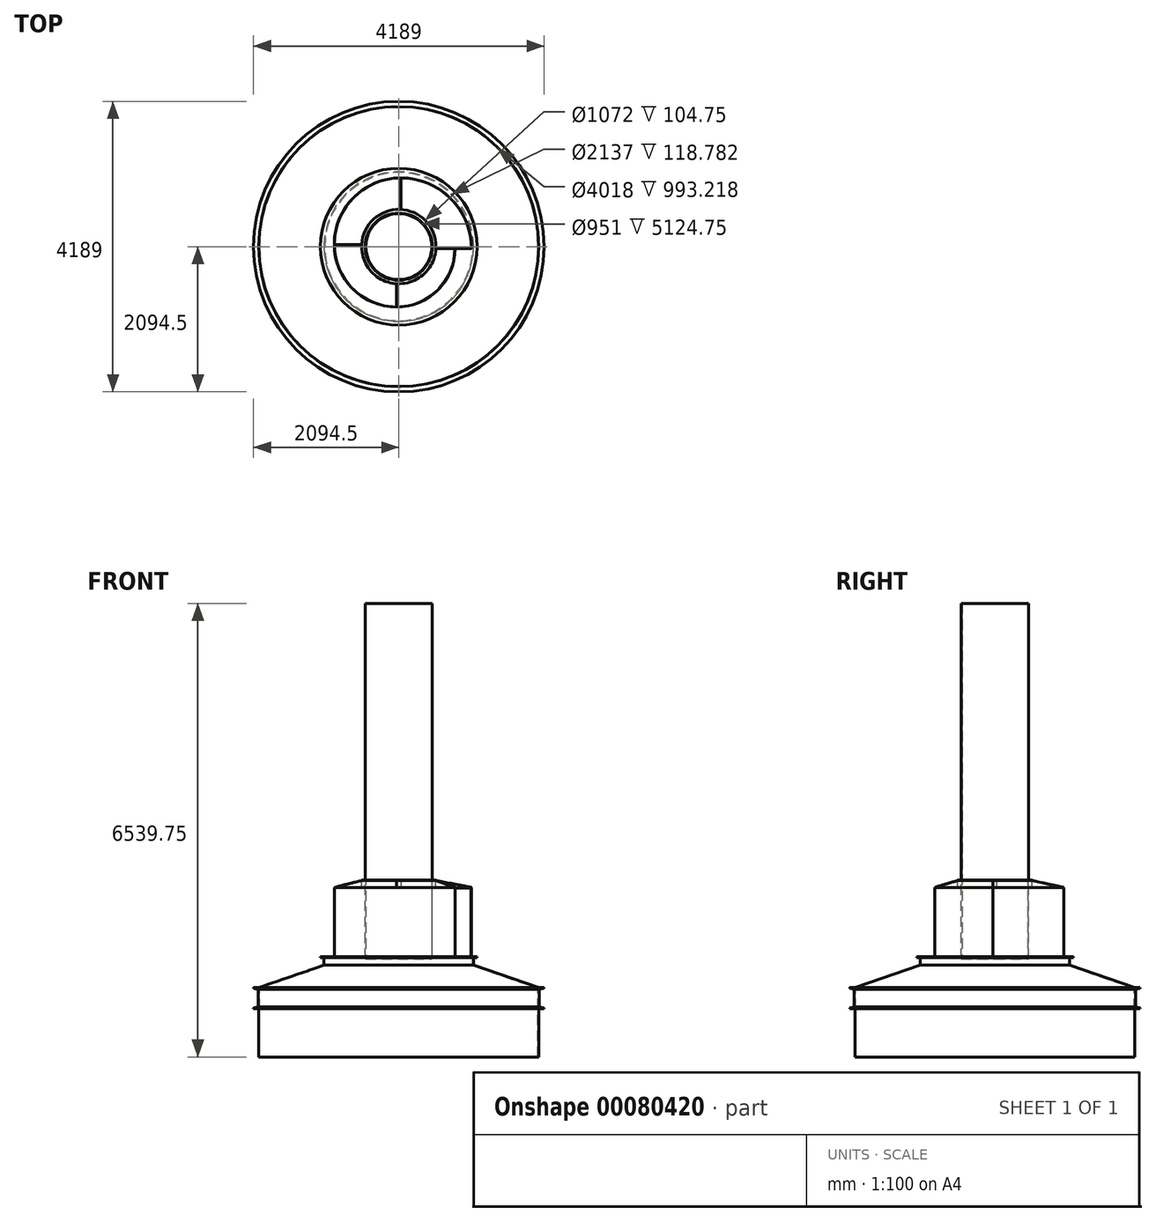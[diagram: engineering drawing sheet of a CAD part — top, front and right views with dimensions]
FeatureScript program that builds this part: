
annotation { "Feature Type Name" : "Feature", "Feature Type Description" : "" }
export const myFeature = defineFeature(function(context is Context, id is Id, definition is map)
    precondition{}
    {
        {
            var Q0;
            Q0=qCreatedBy(makeId("Front.planeOp"),FACE);
            var sketch = newSketch(context, id + "F0", { "sketchPlane" : qUnion([Q0])});
            skLineSegment(sketch, "E0", {"start": v(-2018.5, -1000) * mm, "end": v(-2018.5, 0) * mm});
            skLineSegment(sketch, "E1", {"start": v(-2018.5, 0) * mm, "end": v(-1078, 323) * mm});
            skLineSegment(sketch, "E2", {"start": v(-1078, 323) * mm, "end": v(-1078, 435) * mm});
            skLineSegment(sketch, "E3", {"start": v(0, 444.5) * mm, "end": v(0, -1000) * mm});
            skLineSegment(sketch, "E4", {"start": v(0, -1000) * mm, "end": v(-2018.5, -1000) * mm});
            skLineSegment(sketch, "E5", {"start": v(-1078, 435) * mm, "end": v(-1130, 435) * mm});
            skLineSegment(sketch, "E6", {"start": v(-1130, 435) * mm, "end": v(-1130, 444.5) * mm});
            skLineSegment(sketch, "E7", {"start": v(-1130, 444.5) * mm, "end": v(0, 444.5) * mm});
            skSolve(sketch);
        }
        {
            var Q0;
            Q0 = qSketchRegion(id + "F0", true);
            var Q1;
            Q1=sQuery(id+"F0.wireOp",EDGE,"E3");
            revolve(context, id + "F1", {"entities" : qUnion([Q0]), "axis" : qUnion([Q1]), "revolveType" : RevolveType.FULL});
        }
        {
            var Q0;
            Q0=makeQuery(id+"F1.opRevolve","SWEPT_FACE",FACE,{"disambiguationData":[OSD([sQuery(id+"F0.wireOp",EDGE,"E7")])]});
            var sketch = newSketch(context, id + "F2", { "sketchPlane" : qUnion([Q0])});
            skArc(sketch, "E8", {"start": v(-930, 30) * mm, "mid": v(-666.4, -606.4) * mm, "end": v(-30, -870) * mm});
            skLineSegment(sketch, "E9.bottom", {"start": v(-30, 30) * mm, "end": v(30, 30) * mm, "construction": true});
            skLineSegment(sketch, "E9.top", {"start": v(-30, -30) * mm, "end": v(30, -30) * mm, "construction": true});
            skLineSegment(sketch, "E9.left", {"start": v(-30, 30) * mm, "end": v(-30, -30) * mm, "construction": true});
            skLineSegment(sketch, "E9.right", {"start": v(30, 30) * mm, "end": v(30, -30) * mm, "construction": true});
            skPoint(sketch, "E9.middle", {"position": v(0, 0) * mm});
            skArc(sketch, "E10", {"start": v(-930, 30) * mm, "mid": v(-648.82, 708.82) * mm, "end": v(30, 990) * mm});
            skArc(sketch, "E11", {"start": v(30, 990) * mm, "mid": v(751.25, 691.25) * mm, "end": v(1050, -30) * mm});
            skArc(sketch, "E12", {"start": v(-30, -870) * mm, "mid": v(563.97, -623.97) * mm, "end": v(810, -30) * mm});
            skLineSegment(sketch, "E13", {"start": v(810, -30) * mm, "end": v(1050, -30) * mm});
            skSolve(sketch);
        }
        {
            var Q0;
            Q0 = qSketchRegion(id + "F2", true);
            extrude(context, id + "F3", {"entities" : qUnion([Q0]), "operationType" : NewBodyOperationType.ADD, "depth" : 1000 * mm});
        }
        {
            var Q0;
            Q0=makeQuery(id+"F1.opRevolve","SWEPT_FACE",FACE,{"disambiguationData":[OSD([sQuery(id+"F0.wireOp",EDGE,"E4")])]});
            var Q1;
            Q1=makeQuery(id+"F3.opExtrude","SWEPT_FACE",FACE,{"disambiguationData":[OSD([sQuery(id+"F2.wireOp",EDGE,"E13")])]});
            shell(context, id + "F4", {"entities" : qUnion([Q0, Q1]), "thickness" : 9.5 * mm});
        }
        {
            var Q0;
            Q0=makeQuery(id+"F3.opExtrude","CAP_FACE",FACE,{"disambiguationData":[OSD([sQuery(id+"F2.wireOp",EDGE,"E8"),sQuery(id+"F2.wireOp",EDGE,"E10"),sQuery(id+"F2.wireOp",EDGE,"E11"),sQuery(id+"F2.wireOp",EDGE,"E12"),sQuery(id+"F2.wireOp",EDGE,"E13")])],"isStart":false});
            cPlane(context, id + "F5", {"entities" : qUnion([Q0]), "cplaneType" : CPlaneType.OFFSET, "offset" : 100 * mm, "width" : 150 * mm, "height" : 150 * mm});
        }
        {
            var Q0;
            Q0=qCreatedBy(id+"F5.planeOp",FACE);
            var sketch = newSketch(context, id + "F6", { "sketchPlane" : qUnion([Q0])});
            skPoint(sketch, "E14.0", {"position": v(-30, -870) * mm});
            skPoint(sketch, "E14.1", {"position": v(-930, 30) * mm});
            skPoint(sketch, "E14.2", {"position": v(30, 990) * mm});
            skPoint(sketch, "E14.3", {"position": v(810, -30) * mm});
            skLineSegment(sketch, "E15", {"start": v(30, 990) * mm, "end": v(30, 535.16) * mm, "construction": true});
            skLineSegment(sketch, "E16", {"start": v(-930, 30) * mm, "end": v(-535.16, 30) * mm, "construction": true});
            skLineSegment(sketch, "E17", {"start": v(810, -30) * mm, "end": v(535.16, -30) * mm, "construction": true});
            skLineSegment(sketch, "E18", {"start": v(-30, -870) * mm, "end": v(-30, -535.16) * mm, "construction": true});
            skArc(sketch, "E19", {"start": v(-535.16, 30) * mm, "mid": v(-399.63, -357.2) * mm, "end": v(-30, -535.16) * mm});
            skArc(sketch, "E20", {"start": v(-30, -535.16) * mm, "mid": v(357.2, -399.63) * mm, "end": v(535.16, -30) * mm});
            skArc(sketch, "E21", {"start": v(30, 535.16) * mm, "mid": v(-357.2, 399.63) * mm, "end": v(-535.16, 30) * mm});
            skArc(sketch, "E22", {"start": v(535.16, -30) * mm, "mid": v(399.63, 357.2) * mm, "end": v(30, 535.16) * mm});
            skSolve(sketch);
        }
        {
            var Q0;
            Q0=qCreatedBy(makeId("Right.planeOp"),FACE);
            var Q1;
            Q1=makeQuery(id+"F3.opExtrude","CAP_VERTEX",VERTEX,{"disambiguationData":[OSD([sQuery(id+"F2.wireOp",EDGE,"E8"),sQuery(id+"F2.wireOp",EDGE,"E12")])],"isStart":false});
            cPlane(context, id + "F7", {"entities" : qUnion([Q0, Q1]), "cplaneType" : CPlaneType.PLANE_POINT, "offset" : 25 * mm, "width" : 150 * mm, "height" : 150 * mm});
        }
        {
            var Q0;
            Q0=qCreatedBy(makeId("Front.planeOp"),FACE);
            var Q1;
            Q1=makeQuery(id+"F3.opExtrude","CAP_VERTEX",VERTEX,{"disambiguationData":[OSD([sQuery(id+"F2.wireOp",EDGE,"E8"),sQuery(id+"F2.wireOp",EDGE,"E10")])],"isStart":false});
            cPlane(context, id + "F8", {"entities" : qUnion([Q0, Q1]), "cplaneType" : CPlaneType.PLANE_POINT, "offset" : 25 * mm, "width" : 150 * mm, "height" : 150 * mm});
        }
        {
            var Q0;
            Q0=qCreatedBy(makeId("Right.planeOp"),FACE);
            var Q1;
            Q1=makeQuery(id+"F3.opExtrude","CAP_VERTEX",VERTEX,{"disambiguationData":[OSD([sQuery(id+"F2.wireOp",EDGE,"E10"),sQuery(id+"F2.wireOp",EDGE,"E11")])],"isStart":false});
            cPlane(context, id + "F9", {"entities" : qUnion([Q0, Q1]), "cplaneType" : CPlaneType.PLANE_POINT, "offset" : 25 * mm, "width" : 150 * mm, "height" : 150 * mm});
        }
        {
            var Q0;
            Q0=makeQuery(id+"F3.opExtrude","CAP_FACE",FACE,{"disambiguationData":[OSD([sQuery(id+"F2.wireOp",EDGE,"E8"),sQuery(id+"F2.wireOp",EDGE,"E10"),sQuery(id+"F2.wireOp",EDGE,"E11"),sQuery(id+"F2.wireOp",EDGE,"E12"),sQuery(id+"F2.wireOp",EDGE,"E13")])],"isStart":false});
            var sketch = newSketch(context, id + "F10", { "sketchPlane" : qUnion([Q0])});
            skArc(sketch, "E23.0", {"start": v(-535.16, 30) * mm, "mid": v(-399.63, -357.2) * mm, "end": v(-30, -535.16) * mm});
            skArc(sketch, "E24.0", {"start": v(30, 535.16) * mm, "mid": v(-357.2, 399.63) * mm, "end": v(-535.16, 30) * mm});
            skArc(sketch, "E25.0", {"start": v(535.16, -30) * mm, "mid": v(399.63, 357.2) * mm, "end": v(30, 535.16) * mm});
            skArc(sketch, "E26.0", {"start": v(-30, -535.16) * mm, "mid": v(357.2, -399.63) * mm, "end": v(535.16, -30) * mm});
            skSolve(sketch);
        }
        {
            var Q0;
            Q0=makeQuery(id+"F3.opExtrude","SWEPT_FACE",FACE,{"disambiguationData":[OSD([sQuery(id+"F2.wireOp",EDGE,"E13")])]});
            var sketch = newSketch(context, id + "F11", { "sketchPlane" : qUnion([Q0])});
            skPoint(sketch, "E27.0", {"position": v(535.16, 1544.5) * mm});
            skPoint(sketch, "E28.0", {"position": v(535.16, 1444.5) * mm});
            skPoint(sketch, "E29.0", {"position": v(810, 1444.5) * mm});
            skLineSegment(sketch, "E30", {"start": v(535.16, 1544.5) * mm, "end": v(535.16, 1444.5) * mm});
            skLineSegment(sketch, "E31", {"start": v(810, 1444.5) * mm, "end": v(535.16, 1544.5) * mm});
            skLineSegment(sketch, "E32", {"start": v(535.16, 1444.5) * mm, "end": v(810, 1444.5) * mm});
            skSolve(sketch);
        }
        {
            var Q0;
            Q0=qCreatedBy(id+"F7.planeOp",FACE);
            var sketch = newSketch(context, id + "F12", { "sketchPlane" : qUnion([Q0])});
            skPoint(sketch, "E33.0", {"position": v(-535.16, 1544.5) * mm});
            skPoint(sketch, "E33.1", {"position": v(-535.16, 1444.5) * mm});
            skPoint(sketch, "E33.2", {"position": v(-870, 1444.5) * mm});
            skLineSegment(sketch, "E34", {"start": v(-870, 1444.5) * mm, "end": v(-535.16, 1544.5) * mm});
            skLineSegment(sketch, "E35", {"start": v(-535.16, 1544.5) * mm, "end": v(-535.16, 1444.5) * mm});
            skLineSegment(sketch, "E36", {"start": v(-535.16, 1444.5) * mm, "end": v(-870, 1444.5) * mm});
            skSolve(sketch);
        }
        {
            var Q0;
            Q0=qCreatedBy(id+"F8.planeOp",FACE);
            var sketch = newSketch(context, id + "F13", { "sketchPlane" : qUnion([Q0])});
            skPoint(sketch, "E37.0", {"position": v(-930, 1444.5) * mm});
            skPoint(sketch, "E38.0", {"position": v(-535.16, 1544.5) * mm});
            skPoint(sketch, "E39.0", {"position": v(-535.16, 1444.5) * mm});
            skLineSegment(sketch, "E40", {"start": v(-930, 1444.5) * mm, "end": v(-535.16, 1544.5) * mm});
            skLineSegment(sketch, "E41", {"start": v(-535.16, 1444.5) * mm, "end": v(-535.16, 1544.5) * mm});
            skLineSegment(sketch, "E42", {"start": v(-535.16, 1444.5) * mm, "end": v(-930, 1444.5) * mm});
            skSolve(sketch);
        }
        {
            var Q0;
            Q0=qCreatedBy(id+"F9.planeOp",FACE);
            var sketch = newSketch(context, id + "F14", { "sketchPlane" : qUnion([Q0])});
            skPoint(sketch, "E43.0", {"position": v(535.16, 1544.5) * mm});
            skPoint(sketch, "E44.0", {"position": v(535.16, 1444.5) * mm});
            skPoint(sketch, "E45.0", {"position": v(990, 1444.5) * mm});
            skLineSegment(sketch, "E46", {"start": v(990, 1444.5) * mm, "end": v(535.16, 1444.5) * mm});
            skLineSegment(sketch, "E47", {"start": v(535.16, 1544.5) * mm, "end": v(535.16, 1444.5) * mm});
            skLineSegment(sketch, "E48", {"start": v(535.16, 1544.5) * mm, "end": v(990, 1444.5) * mm});
            skSolve(sketch);
        }
        {
            var Q0;
            {var subQ0=sQuery(id+"F2.wireOp",EDGE,"E13");var subQ2=makeQuery(id+"F3.opExtrude","CAP_EDGE",EDGE,{"disambiguationData":[OSD([subQ0])],"isStart":false});Q0=makeQuery(id+"F11.imprint","IMPRINT",FACE,{"disambiguationData":[TD([[makeQuery(id+"F11.imprint","IMPRINT",EDGE,{"derivedFrom":subQ2}),-1.0]])]});}
            var sketch = newSketch(context, id + "F15", { "sketchPlane" : qUnion([Q0])});
            skPoint(sketch, "E49.0", {"position": v(1050, 1444.5) * mm});
            skPoint(sketch, "E50.0", {"position": v(535.16, 1544.5) * mm});
            skPoint(sketch, "E51.0", {"position": v(535.16, 1444.5) * mm});
            skLineSegment(sketch, "E52", {"start": v(535.16, 1544.5) * mm, "end": v(1050, 1444.5) * mm});
            skLineSegment(sketch, "E53", {"start": v(535.16, 1444.5) * mm, "end": v(535.16, 1544.5) * mm});
            skLineSegment(sketch, "E54", {"start": v(535.16, 1444.5) * mm, "end": v(1050, 1444.5) * mm});
            skSolve(sketch);
        }
        {
            var Q1;
            Q1=makeQuery(id+"F11.imprint","IMPRINT",FACE,{"disambiguationData":[TD([[makeQuery(id+"F11.imprint","IMPRINT",EDGE,{"derivedFrom":sQuery(id+"F11.wireOp",EDGE,"E30")}),1.0]])]});
            var Q2;
            Q2=makeQuery(id+"F12.imprint","IMPRINT",FACE,{"disambiguationData":[TD([[makeQuery(id+"F12.imprint","IMPRINT",EDGE,{"derivedFrom":sQuery(id+"F12.wireOp",EDGE,"E34")}),-1.0]])]});
            var Q3;
            Q3=makeQuery(id+"F3.opExtrude","CAP_EDGE",EDGE,{"disambiguationData":[OSD([sQuery(id+"F2.wireOp",EDGE,"E12")])],"isStart":false});
            var Q4;
            Q4=sQuery(id+"F10.wireOp",EDGE,"E26.0");
            var Q5;
            Q5=sQuery(id+"F6.wireOp",EDGE,"E20");
            loft(context, id + "F16", {"operationType" : NewBodyOperationType.ADD, "addGuides" : true, "sheetProfilesArray" : [{ "sheetProfileEntities" : qUnion([Q1]) }, { "sheetProfileEntities" : qUnion([Q2]) }], "guidesArray" : [{ "guideEntities" : qUnion([Q3]), "guideDerivativeType" : LoftGuideDerivativeType.DEFAULT, "guideDerivativeMagnitude" : 1 }, { "guideEntities" : qUnion([Q4]), "guideDerivativeType" : LoftGuideDerivativeType.DEFAULT, "guideDerivativeMagnitude" : 1 }, { "guideEntities" : qUnion([Q5]), "guideDerivativeType" : LoftGuideDerivativeType.DEFAULT, "guideDerivativeMagnitude" : 1 }]});
        }
        {
            var Q1;
            Q1=makeQuery(id+"F16.opLoft","CAP_FACE",FACE,{"disambiguationData":[OSD([makeQuery(id+"F12.imprint","IMPRINT",FACE,{"disambiguationData":[TD([[makeQuery(id+"F12.imprint","IMPRINT",EDGE,{"derivedFrom":sQuery(id+"F12.wireOp",EDGE,"E34")}),-1.0]])]})])],"isStart":true});
            var Q2;
            Q2=makeQuery(id+"F13.imprint","IMPRINT",FACE,{"disambiguationData":[TD([[makeQuery(id+"F13.imprint","IMPRINT",EDGE,{"derivedFrom":sQuery(id+"F13.wireOp",EDGE,"E40")}),-1.0]])]});
            var Q3;
            Q3=sQuery(id+"F10.wireOp",EDGE,"E23.0");
            var Q4;
            Q4=sQuery(id+"F6.wireOp",EDGE,"E19");
            var Q5;
            Q5=makeQuery(id+"F3.opExtrude","CAP_EDGE",EDGE,{"disambiguationData":[OSD([sQuery(id+"F2.wireOp",EDGE,"E8")])],"isStart":false});
            loft(context, id + "F17", {"operationType" : NewBodyOperationType.ADD, "addGuides" : true, "sheetProfilesArray" : [{ "sheetProfileEntities" : qUnion([Q1]) }, { "sheetProfileEntities" : qUnion([Q2]) }], "guidesArray" : [{ "guideEntities" : qUnion([Q3]), "guideDerivativeType" : LoftGuideDerivativeType.DEFAULT, "guideDerivativeMagnitude" : 1 }, { "guideEntities" : qUnion([Q4]), "guideDerivativeType" : LoftGuideDerivativeType.DEFAULT, "guideDerivativeMagnitude" : 1 }, { "guideEntities" : qUnion([Q5]), "guideDerivativeType" : LoftGuideDerivativeType.DEFAULT, "guideDerivativeMagnitude" : 1 }]});
        }
        {
            var Q1;
            Q1=makeQuery(id+"F17.opLoft","CAP_FACE",FACE,{"disambiguationData":[OSD([makeQuery(id+"F13.imprint","IMPRINT",FACE,{"disambiguationData":[TD([[makeQuery(id+"F13.imprint","IMPRINT",EDGE,{"derivedFrom":sQuery(id+"F13.wireOp",EDGE,"E40")}),-1.0]])]})])],"isStart":true});
            var Q2;
            Q2=makeQuery(id+"F14.imprint","IMPRINT",FACE,{"disambiguationData":[TD([[makeQuery(id+"F14.imprint","IMPRINT",EDGE,{"derivedFrom":sQuery(id+"F14.wireOp",EDGE,"E46")}),-1.0]])]});
            var Q3;
            Q3=sQuery(id+"F10.wireOp",EDGE,"E24.0");
            var Q4;
            Q4=sQuery(id+"F6.wireOp",EDGE,"E21");
            var Q5;
            Q5=makeQuery(id+"F3.opExtrude","CAP_EDGE",EDGE,{"disambiguationData":[OSD([sQuery(id+"F2.wireOp",EDGE,"E10")])],"isStart":false});
            loft(context, id + "F18", {"operationType" : NewBodyOperationType.ADD, "addGuides" : true, "sheetProfilesArray" : [{ "sheetProfileEntities" : qUnion([Q1]) }, { "sheetProfileEntities" : qUnion([Q2]) }], "guidesArray" : [{ "guideEntities" : qUnion([Q3]), "guideDerivativeType" : LoftGuideDerivativeType.DEFAULT, "guideDerivativeMagnitude" : 1 }, { "guideEntities" : qUnion([Q4]), "guideDerivativeType" : LoftGuideDerivativeType.DEFAULT, "guideDerivativeMagnitude" : 1 }, { "guideEntities" : qUnion([Q5]), "guideDerivativeType" : LoftGuideDerivativeType.DEFAULT, "guideDerivativeMagnitude" : 1 }]});
        }
        {
            var Q1;
            Q1=makeQuery(id+"F18.opLoft","CAP_FACE",FACE,{"disambiguationData":[OSD([makeQuery(id+"F14.imprint","IMPRINT",FACE,{"disambiguationData":[TD([[makeQuery(id+"F14.imprint","IMPRINT",EDGE,{"derivedFrom":sQuery(id+"F14.wireOp",EDGE,"E46")}),-1.0]])]})])],"isStart":true});
            var Q2;
            {var subQ0=sQuery(id+"F15.wireOp",EDGE,"E52");Q2=makeQuery(id+"F15.imprint","IMPRINT",FACE,{"disambiguationData":[TD([[makeQuery(id+"F15.imprint","IMPRINT",EDGE,{"derivedFrom":subQ0}),-1.0]])]});}
            var Q3;
            Q3=sQuery(id+"F10.wireOp",EDGE,"E25.0");
            var Q4;
            Q4=sQuery(id+"F6.wireOp",EDGE,"E22");
            var Q5;
            Q5=makeQuery(id+"F3.opExtrude","CAP_EDGE",EDGE,{"disambiguationData":[OSD([sQuery(id+"F2.wireOp",EDGE,"E11")])],"isStart":false});
            loft(context, id + "F19", {"operationType" : NewBodyOperationType.ADD, "addGuides" : true, "sheetProfilesArray" : [{ "sheetProfileEntities" : qUnion([Q1]) }, { "sheetProfileEntities" : qUnion([Q2]) }], "guidesArray" : [{ "guideEntities" : qUnion([Q3]), "guideDerivativeType" : LoftGuideDerivativeType.DEFAULT, "guideDerivativeMagnitude" : 1 }, { "guideEntities" : qUnion([Q4]), "guideDerivativeType" : LoftGuideDerivativeType.DEFAULT, "guideDerivativeMagnitude" : 1 }, { "guideEntities" : qUnion([Q5]), "guideDerivativeType" : LoftGuideDerivativeType.DEFAULT, "guideDerivativeMagnitude" : 1 }]});
        }
        {
            var Q0;
            Q0=makeQuery(id+"F3.opExtrude","CAP_FACE",FACE,{"disambiguationData":[OSD([sQuery(id+"F2.wireOp",EDGE,"E8"),sQuery(id+"F2.wireOp",EDGE,"E10"),sQuery(id+"F2.wireOp",EDGE,"E11"),sQuery(id+"F2.wireOp",EDGE,"E12"),sQuery(id+"F2.wireOp",EDGE,"E13")])],"isStart":false});
            extrude(context, id + "F20", {"entities" : qUnion([Q0]), "operationType" : NewBodyOperationType.REMOVE, "endBound" : BoundingType.UP_TO_NEXT, "oppositeDirection" : true, "depth" : 25 * mm});
        }
        {
            var Q0;
            Q0=qCreatedBy(id+"F5.planeOp",FACE);
            var sketch = newSketch(context, id + "F21", { "sketchPlane" : qUnion([Q0])});
            skArc(sketch, "E55.0", {"start": v(-535.16, 30) * mm, "mid": v(-357.2, 399.63) * mm, "end": v(30, 535.16) * mm});
            skArc(sketch, "E56.0", {"start": v(30, 535.16) * mm, "mid": v(399.63, 357.2) * mm, "end": v(535.16, -30) * mm});
            skArc(sketch, "E57.0", {"start": v(535.16, -30) * mm, "mid": v(357.2, -399.63) * mm, "end": v(-30, -535.16) * mm});
            skArc(sketch, "E58.0", {"start": v(-30, -535.16) * mm, "mid": v(-399.63, -357.2) * mm, "end": v(-535.16, 30) * mm});
            skCircle(sketch, "E59", {"center": v(0, 0) * mm, "radius": 485 * mm});
            skSolve(sketch);
        }
        {
            var Q0;
            Q0 = qSketchRegion(id + "F21", true);
            extrude(context, id + "F22", {"entities" : qUnion([Q0]), "operationType" : NewBodyOperationType.ADD, "endBound" : BoundingType.SYMMETRIC, "depth" : 9.5 * mm});
        }
        {
            var Q0;
            Q0=makeQuery(id+"F22.opExtrude","CAP_FACE",FACE,{"disambiguationData":[OSD([sQuery(id+"F21.wireOp",EDGE,"E55.0"),sQuery(id+"F21.wireOp",EDGE,"E56.0"),sQuery(id+"F21.wireOp",EDGE,"E57.0"),sQuery(id+"F21.wireOp",EDGE,"E58.0"),sQuery(id+"F21.wireOp",EDGE,"E59")])],"isStart":true});
            var sketch = newSketch(context, id + "F23", { "sketchPlane" : qUnion([Q0])});
            skCircle(sketch, "E60.0", {"center": v(0, 0) * mm, "radius": 485 * mm});
            skCircle(sketch, "E61", {"center": v(0, 0) * mm, "radius": 475.5 * mm});
            skSolve(sketch);
        }
        {
            var Q0;
            Q0 = qSketchRegion(id + "F23", true);
            extrude(context, id + "F24", {"entities" : qUnion([Q0]), "operationType" : NewBodyOperationType.ADD, "oppositeDirection" : true, "depth" : 4000 * mm});
        }
        {
            var Q0;
            Q0 = qSketchRegion(id + "F23", true);
            extrude(context, id + "F25", {"entities" : qUnion([Q0]), "operationType" : NewBodyOperationType.ADD, "depth" : (1220 - 95.25) * mm});
        }
        {
            var Q0;
            Q0=qCreatedBy(makeId("Front.planeOp"),FACE);
            var sketch = newSketch(context, id + "F26", { "sketchPlane" : qUnion([Q0])});
            skLineSegment(sketch, "E62.0", {"start": v(-2018.5, 0) * mm, "end": v(2018.5, 0) * mm, "construction": true});
            skLineSegment(sketch, "E63", {"start": v(2018.5, 0) * mm, "end": v(2018.5, -152.4) * mm});
            skLineSegment(sketch, "E64", {"start": v(2018.5, 0) * mm, "end": v(2094.5, 0) * mm});
            skLineSegment(sketch, "E65", {"start": v(2028, -27) * mm, "end": v(2028, -152.4) * mm});
            skLineSegment(sketch, "E66", {"start": v(2018.5, -152.4) * mm, "end": v(2028, -152.4) * mm, "construction": true});
            skArc(sketch, "E67", {"start": v(2085.63, -11.56) * mm, "mid": v(2092.03, -7.28) * mm, "end": v(2094.5, 0) * mm});
            skLineSegment(sketch, "E68", {"start": v(2028, -27) * mm, "end": v(2085.63, -11.56) * mm});
            skLineSegment(sketch, "E69", {"start": v(2094.5, 0) * mm, "end": v(2094.5, -152.4) * mm, "construction": true});
            skLineSegment(sketch, "E70.MirrorCS", {"start": v(2028, -277.8) * mm, "end": v(2028, -152.4) * mm});
            skLineSegment(sketch, "E71.MirrorCS", {"start": v(2028, -277.8) * mm, "end": v(2085.63, -293.24) * mm});
            skArc(sketch, "E72.MirrorCS", {"start": v(2085.63, -293.24) * mm, "mid": v(2092.03, -297.52) * mm, "end": v(2094.5, -304.8) * mm});
            skLineSegment(sketch, "E73.MirrorCS", {"start": v(2018.5, -304.8) * mm, "end": v(2094.5, -304.8) * mm});
            skLineSegment(sketch, "E74.MirrorCS", {"start": v(2018.5, -304.8) * mm, "end": v(2018.5, -152.4) * mm});
            skSolve(sketch);
        }
        {
            var Q0;
            Q0=makeQuery(id+"F26.imprint","IMPRINT",FACE,{"disambiguationData":[TD([[makeQuery(id+"F26.imprint","IMPRINT",EDGE,{"derivedFrom":sQuery(id+"F26.wireOp",EDGE,"E63")}),1.0]])]});
            var Q1;
            Q1=makeQuery(id+"F1.opRevolve","SWEPT_FACE",FACE,{"disambiguationData":[OSD([sQuery(id+"F0.wireOp",EDGE,"E0")])]});
            revolve(context, id + "F27", {"operationType" : NewBodyOperationType.ADD, "entities" : qUnion([Q0]), "axis" : qUnion([Q1]), "revolveType" : RevolveType.FULL});
        }
    });
